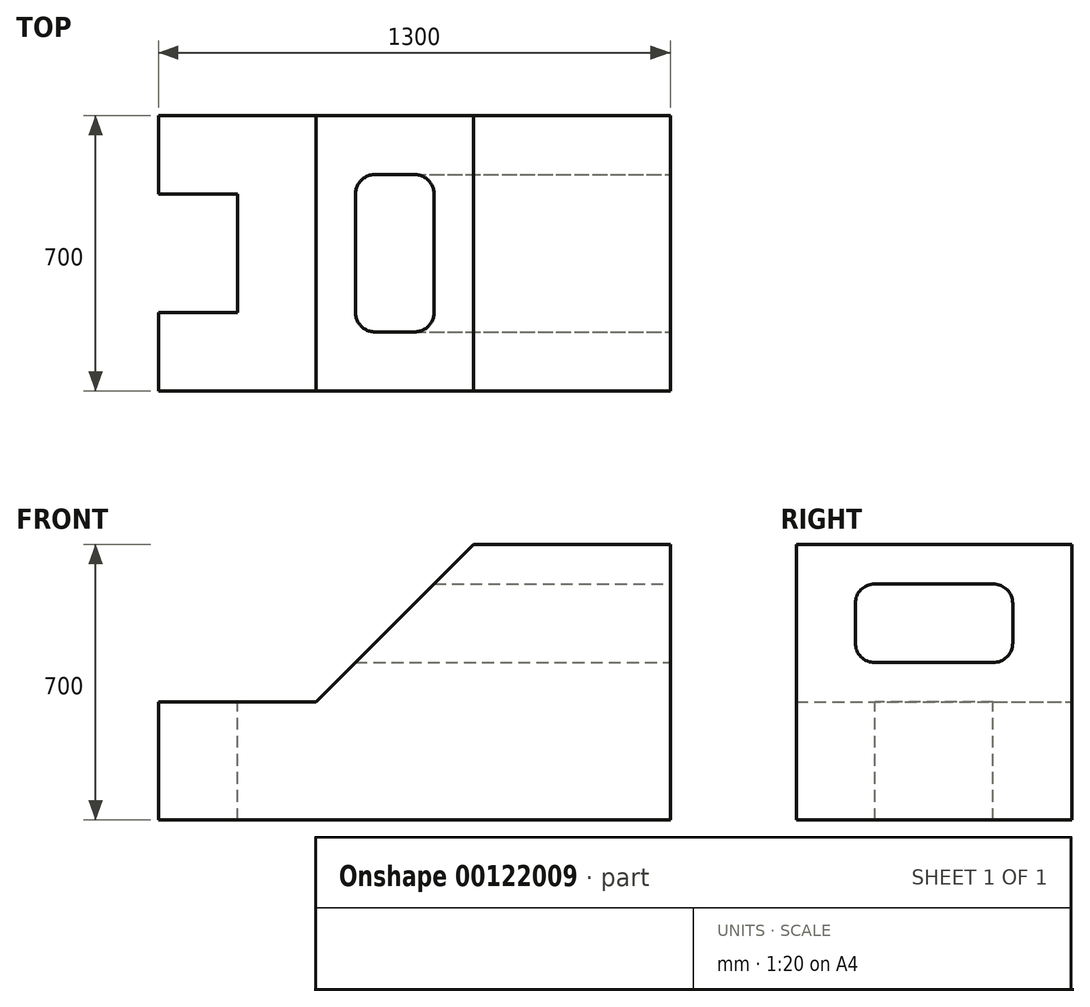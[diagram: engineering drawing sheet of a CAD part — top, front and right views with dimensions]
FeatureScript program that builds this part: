
annotation { "Feature Type Name" : "Feature", "Feature Type Description" : "" }
export const myFeature = defineFeature(function(context is Context, id is Id, definition is map)
    precondition{}
    {
        {
            var Q0;
            Q0=qCreatedBy(makeId("Front.planeOp"),FACE);
            var sketch = newSketch(context, id + "F0", { "sketchPlane" : qUnion([Q0])});
            skLineSegment(sketch, "E0.bottom", {"start": v(150, 350) * mm, "end": v(650, 350) * mm});
            skLineSegment(sketch, "E0.top", {"start": v(-650, -350) * mm, "end": v(650, -350) * mm});
            skLineSegment(sketch, "E0.left", {"start": v(-650, -50) * mm, "end": v(-650, -350) * mm});
            skLineSegment(sketch, "E0.right", {"start": v(650, 350) * mm, "end": v(650, -350) * mm});
            skPoint(sketch, "E0.middle", {"position": v(0, 0) * mm});
            skLineSegment(sketch, "E1", {"start": v(650, 350) * mm, "end": v(150, 350) * mm});
            skLineSegment(sketch, "E2", {"start": v(150, 350) * mm, "end": v(-250, -50) * mm});
            skLineSegment(sketch, "E3", {"start": v(-250, -50) * mm, "end": v(-650, -50) * mm});
            skPoint(sketch, "E4.orphan", {"position": v(-650, 350) * mm});
            skSolve(sketch);
        }
        {
            var Q0;
            Q0 = qSketchRegion(id + "F0", true);
            extrude(context, id + "F1", {"entities" : qUnion([Q0]), "depth" : 700 * mm});
        }
        {
            var Q0;
            Q0=makeQuery(id+"F1.opExtrude","SWEPT_FACE",FACE,{"disambiguationData":[OSD([sQuery(id+"F0.wireOp",EDGE,"E0.right")])]});
            var sketch = newSketch(context, id + "F2", { "sketchPlane" : qUnion([Q0])});
            skLineSegment(sketch, "E5.bottom", {"start": v(-500, 250) * mm, "end": v(-200, 250) * mm});
            skLineSegment(sketch, "E5.top", {"start": v(-500, 50) * mm, "end": v(-200, 50) * mm});
            skLineSegment(sketch, "E5.left", {"start": v(-550, 200) * mm, "end": v(-550, 100) * mm});
            skLineSegment(sketch, "E5.right", {"start": v(-150, 200) * mm, "end": v(-150, 100) * mm});
            skPoint(sketch, "E6.visualSharp", {"position": v(-550, 250) * mm});
            skArc(sketch, "E6.filletArc", {"start": v(-500, 250) * mm, "mid": v(-535.36, 235.36) * mm, "end": v(-550, 200) * mm});
            skPoint(sketch, "E7.visualSharp", {"position": v(-550, 50) * mm});
            skArc(sketch, "E7.filletArc", {"start": v(-550, 100) * mm, "mid": v(-535.36, 64.64) * mm, "end": v(-500, 50) * mm});
            skPoint(sketch, "E8.visualSharp", {"position": v(-150, 50) * mm});
            skArc(sketch, "E8.filletArc", {"start": v(-200, 50) * mm, "mid": v(-164.64, 64.64) * mm, "end": v(-150, 100) * mm});
            skPoint(sketch, "E9.visualSharp", {"position": v(-150, 250) * mm});
            skArc(sketch, "E9.filletArc", {"start": v(-150, 200) * mm, "mid": v(-164.64, 235.36) * mm, "end": v(-200, 250) * mm});
            skSolve(sketch);
        }
        {
            var Q0;
            Q0 = qSketchRegion(id + "F2", true);
            extrude(context, id + "F3", {"entities" : qUnion([Q0]), "operationType" : NewBodyOperationType.REMOVE, "endBound" : BoundingType.THROUGH_ALL, "oppositeDirection" : true, "depth" : 25.4 * mm});
        }
        {
            var Q0;
            Q0=makeQuery(id+"F1.opExtrude","SWEPT_FACE",FACE,{"disambiguationData":[OSD([sQuery(id+"F0.wireOp",EDGE,"E3")])]});
            var sketch = newSketch(context, id + "F4", { "sketchPlane" : qUnion([Q0])});
            skLineSegment(sketch, "E10.bottom", {"start": v(-450, -200) * mm, "end": v(-650, -200) * mm});
            skLineSegment(sketch, "E10.top", {"start": v(-450, -500) * mm, "end": v(-650, -500) * mm});
            skLineSegment(sketch, "E10.left", {"start": v(-450, -200) * mm, "end": v(-450, -500) * mm});
            skPoint(sketch, "E10.middle", {"position": v(-650, -350) * mm});
            skLineSegment(sketch, "E11", {"start": v(-650, -200) * mm, "end": v(-650, -500) * mm});
            skPoint(sketch, "E12.orphan", {"position": v(-850, -200) * mm});
            skPoint(sketch, "E13.orphan", {"position": v(-850, -500) * mm});
            skSolve(sketch);
        }
        {
            var Q0;
            Q0 = qSketchRegion(id + "F4", true);
            extrude(context, id + "F5", {"entities" : qUnion([Q0]), "operationType" : NewBodyOperationType.REMOVE, "endBound" : BoundingType.THROUGH_ALL, "oppositeDirection" : true, "depth" : 25.4 * mm});
        }
    });
